# Revit family: 0005379
name_source: partatom
category: Lighting Fixtures
revit_build: Autodesk Revit 2016 (Build: 20150220_1215(x64)
units: mm (PartAtom-declared; Revit-internal decimal feet)

## family parameters
Cut with Voids When Loaded = No
Host = Face
Light Source = Yes
OmniClass Number = 23.80.70.00
OmniClass Title = Lighting
Part Type = Normal
Room Calculation Point = No
Round Connector Dimension = Use Diameter
Shared = No

## types (1)
- 0005379 START eco Spot 540lm 830 IP65 DIM WHT
    Apparent Load = 7 VA
    Assembly Code = D5020200
    AssetType = Fixed
    ClassificationName = Uniclass2015
    ClassificationValue = EF_70_80
    Color Filter = 16777215
    Cost = 0 $
    Default Elevation = 1219 mm
    Dimming Lamp Color Temperature Shift = <None>
    DimmingControlOptions = Dimmable
    DocumentationLiterature = http://www.sylvania-lighting.com
    ElectricShockClassification = Class II
    Emit Shape Visible in Rendering = No
    Emit from Circle Diameter = 54 mm  [stored 0.177165 ft]
    IfcExportAs = IfcLightFixtureType
    IfcExportType = IfcLightFixtureType
    ImpactProtectionIndex = IK03
    IngressProtection = IP20/IP65
    InputNominalFrequency = 50/60/Hz
    InputVoltage = 220-240 V~
    Keynote = 16500
    Lamp = LED
    LampColourTemperature = 3000 K
    LampsType = LED
    LuminousEfficacy = 77.14 lm/W
    Manufacturer = Feilo Sylvania
    ManufacturerName = Feilo Sylvania
    Material_1_SYL = Plastic, Opaque White
    Material_2_SYL = Diffuser-Sylvania
    Material_3_SYL = <By Category>
    Material_4_SYL = <By Category>
    Model = Start eco Spot 540lm 830 IP65 DIM WHT
    ModelNumber = 0005379
    ModelReference = Start eco Spot 540lm 830 IP65 DIM WHT
    Name = Start eco Spot 540lm 830 IP65 DIM WHT
    NominalDepth = 87 mm  [stored 0.285433 ft]
    NominalHeight = 47 mm  [stored 0.154199 ft]
    NominalLength = 87 mm  [stored 0.285433 ft]
    Photometric Web File = 0005379.ies
    PowerConsumption = 7 W
    PowerFactor = 0
    Tilt Angle = -90.00°
    Type Image = <None>
    TypeName = Start eco Spot 540lm 830 IP65 DIM WHT
    URL = http://www.sylvania-lighting.com
    Voltage = 230 V

note: [stored X ft] marks values corroborated as IEEE doubles in the binary element streams (Revit-internal decimal feet)

## geometry (parser evidence)
native form markers: Sweep x1
no freeform markers — native parametric forms only
